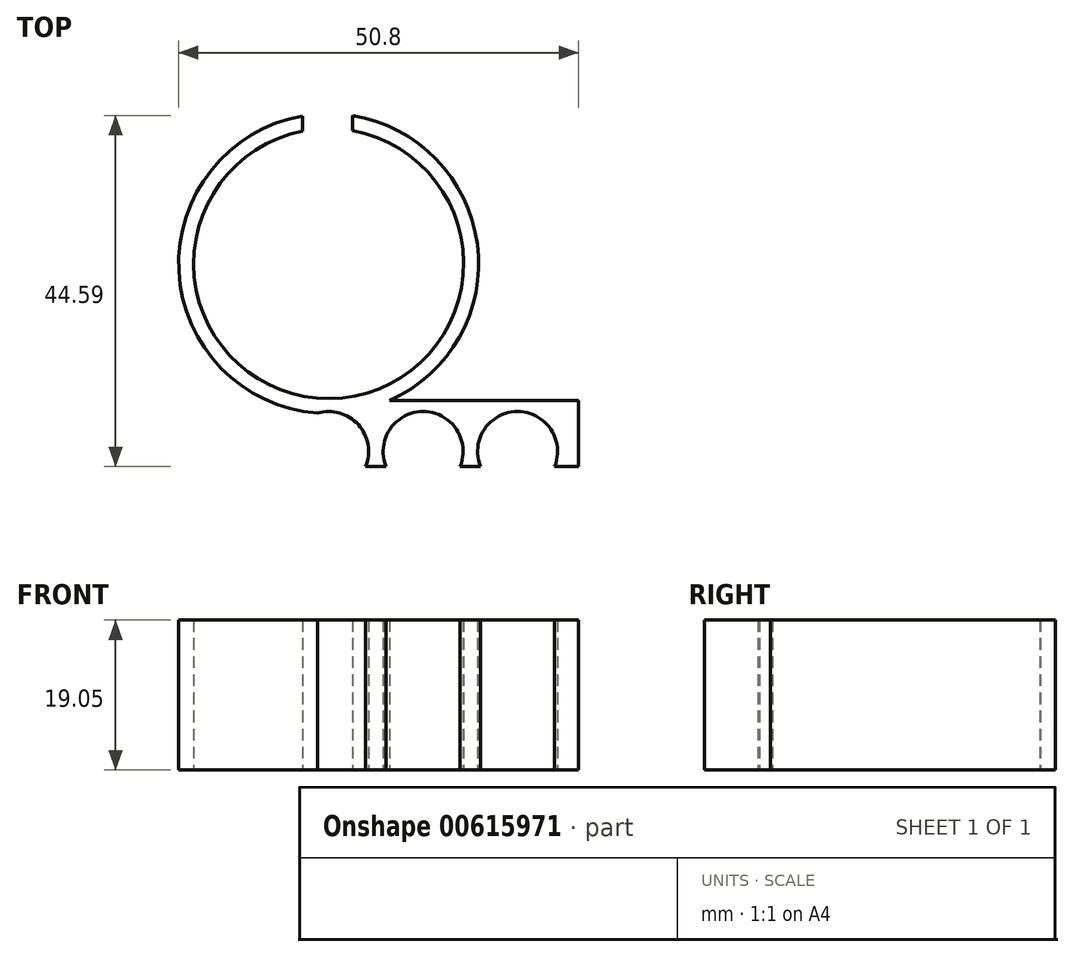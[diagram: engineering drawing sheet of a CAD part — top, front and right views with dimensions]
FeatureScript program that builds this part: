
annotation { "Feature Type Name" : "Feature", "Feature Type Description" : "" }
export const myFeature = defineFeature(function(context is Context, id is Id, definition is map)
    precondition{}
    {
        {
            var Q0;
            Q0=qCreatedBy(makeId("Top.planeOp"),FACE);
            var sketch = newSketch(context, id + "F0", { "sketchPlane" : qUnion([Q0])});
            skCircle(sketch, "E0", {"center": v(0, 0) * mm, "radius": 19.05 * mm});
            skCircle(sketch, "E1", {"center": v(0, 0) * mm, "radius": 17.15 * mm});
            skLineSegment(sketch, "E2.bottom", {"start": v(31.75, -17.4) * mm, "end": v(-31.75, -17.4) * mm});
            skLineSegment(sketch, "E2.top", {"start": v(31.75, -25.78) * mm, "end": v(-31.75, -25.78) * mm});
            skLineSegment(sketch, "E2.left", {"start": v(31.75, -17.4) * mm, "end": v(31.75, -25.78) * mm});
            skLineSegment(sketch, "E2.right", {"start": v(-31.75, -17.4) * mm, "end": v(-31.75, -25.78) * mm});
            skPoint(sketch, "E2.middle", {"position": v(0, -21.59) * mm});
            skCircle(sketch, "E3", {"center": v(0, -23.88) * mm, "radius": 5.08 * mm});
            skPoint(sketch, "E3.centerSnap0", {"position": v(0, -25.78) * mm});
            skCircle(sketch, "E4.1.0.0", {"center": v(12, -23.88) * mm, "radius": 5.08 * mm});
            skCircle(sketch, "E4.2.0.0", {"center": v(24, -23.88) * mm, "radius": 5.08 * mm});
            skLineSegment(sketch, "E4.direction1", {"start": v(0, -23.88) * mm, "end": v(12, -23.88) * mm, "construction": true});
            skCircle(sketch, "E5.1.0.0", {"center": v(-12, -23.88) * mm, "radius": 5.08 * mm});
            skCircle(sketch, "E5.2.0.0", {"center": v(-24, -23.88) * mm, "radius": 5.08 * mm});
            skLineSegment(sketch, "E5.direction1", {"start": v(0, -23.88) * mm, "end": v(-12, -23.88) * mm, "construction": true});
            skSolve(sketch);
        }
        {
            var Q0;
            Q0=makeQuery(id+"F0.imprint","IMPRINT",FACE,{"disambiguationData":[TD([[makeQuery(id+"F0.imprint","IMPRINT",EDGE,{"derivedFrom":sQuery(id+"F0.wireOp",EDGE,"E1")}),-1.0]])]});
            var Q1;
            {var subQ0=sQuery(id+"F0.wireOp",EDGE,"E2.bottom");var subQ1=sQuery(id+"F0.wireOp",EDGE,"E0");var subQ2=makeQuery(id+"F0.imprint","INTERSECT",VERTEX,{"disambiguationData":[OD(0.0)],"derivedFrom":[subQ1,subQ0]});Q1=makeQuery(id+"F0.imprint","IMPRINT",FACE,{"disambiguationData":[TD([[makeQuery(id+"F0.imprint","IMPRINT",EDGE,{"disambiguationData":[TD([[subQ2,-1.0]])],"derivedFrom":subQ1}),1.0]])]});}
            var Q2;
            {var subQ0=sQuery(id+"F0.wireOp",EDGE,"E2.left");Q2=makeQuery(id+"F0.imprint","IMPRINT",FACE,{"disambiguationData":[TD([[makeQuery(id+"F0.imprint","IMPRINT",EDGE,{"derivedFrom":subQ0}),-1.0]])]});}
            var Q3;
            {var subQ8=sQuery(id+"F0.wireOp",EDGE,"E2.right");Q3=makeQuery(id+"F0.imprint","IMPRINT",FACE,{"disambiguationData":[TD([[makeQuery(id+"F0.imprint","IMPRINT",EDGE,{"derivedFrom":subQ8}),1.0]])]});}
            extrude(context, id + "F1", {"entities" : qUnion([Q0, Q1, Q2, Q3]), "depth" : 19.05 * mm, "offsetDistance" : 25 * mm});
        }
        {
            var Q0;
            {var subQ0=sQuery(id+"F0.wireOp",EDGE,"E4.3.0.0");var subQ1=sQuery(id+"F0.wireOp",EDGE,"E2.top");var subQ2=makeQuery(id+"F0.imprint","INTERSECT",VERTEX,{"disambiguationData":[OD(0.0)],"derivedFrom":[subQ1,subQ0]});Q0=makeQuery(id+"F0.imprint","IMPRINT",FACE,{"disambiguationData":[TD([[makeQuery(id+"F0.imprint","IMPRINT",EDGE,{"disambiguationData":[TD([[subQ2,-1.0]])],"derivedFrom":subQ1}),-1.0]])]});}
            var Q1;
            {var subQ0=sQuery(id+"F0.wireOp",EDGE,"E4.2.0.0");var subQ1=sQuery(id+"F0.wireOp",EDGE,"E2.top");var subQ2=makeQuery(id+"F0.imprint","INTERSECT",VERTEX,{"disambiguationData":[OD(0.0)],"derivedFrom":[subQ1,subQ0]});Q1=makeQuery(id+"F0.imprint","IMPRINT",FACE,{"disambiguationData":[TD([[makeQuery(id+"F0.imprint","IMPRINT",EDGE,{"disambiguationData":[TD([[subQ2,-1.0]])],"derivedFrom":subQ1}),-1.0]])]});}
            var Q2;
            {var subQ0=sQuery(id+"F0.wireOp",EDGE,"E4.1.0.0");var subQ1=sQuery(id+"F0.wireOp",EDGE,"E2.top");var subQ2=makeQuery(id+"F0.imprint","INTERSECT",VERTEX,{"disambiguationData":[OD(0.0)],"derivedFrom":[subQ1,subQ0]});Q2=makeQuery(id+"F0.imprint","IMPRINT",FACE,{"disambiguationData":[TD([[makeQuery(id+"F0.imprint","IMPRINT",EDGE,{"disambiguationData":[TD([[subQ2,-1.0]])],"derivedFrom":subQ1}),-1.0]])]});}
            var Q3;
            {var subQ0=sQuery(id+"F0.wireOp",EDGE,"E3");var subQ1=sQuery(id+"F0.wireOp",EDGE,"E2.top");var subQ2=makeQuery(id+"F0.imprint","INTERSECT",VERTEX,{"disambiguationData":[OD(0.0)],"derivedFrom":[subQ1,subQ0]});Q3=makeQuery(id+"F0.imprint","IMPRINT",FACE,{"disambiguationData":[TD([[makeQuery(id+"F0.imprint","IMPRINT",EDGE,{"disambiguationData":[TD([[subQ2,-1.0]])],"derivedFrom":subQ1}),-1.0]])]});}
            var Q4;
            {var subQ0=sQuery(id+"F0.wireOp",EDGE,"E5.1.0.0");var subQ1=sQuery(id+"F0.wireOp",EDGE,"E2.top");var subQ2=makeQuery(id+"F0.imprint","INTERSECT",VERTEX,{"disambiguationData":[OD(0.0)],"derivedFrom":[subQ1,subQ0]});Q4=makeQuery(id+"F0.imprint","IMPRINT",FACE,{"disambiguationData":[TD([[makeQuery(id+"F0.imprint","IMPRINT",EDGE,{"disambiguationData":[TD([[subQ2,-1.0]])],"derivedFrom":subQ1}),-1.0]])]});}
            var Q5;
            {var subQ0=sQuery(id+"F0.wireOp",EDGE,"E5.2.0.0");var subQ1=sQuery(id+"F0.wireOp",EDGE,"E2.top");var subQ2=makeQuery(id+"F0.imprint","INTERSECT",VERTEX,{"disambiguationData":[OD(0.0)],"derivedFrom":[subQ1,subQ0]});Q5=makeQuery(id+"F0.imprint","IMPRINT",FACE,{"disambiguationData":[TD([[makeQuery(id+"F0.imprint","IMPRINT",EDGE,{"disambiguationData":[TD([[subQ2,-1.0]])],"derivedFrom":subQ1}),-1.0]])]});}
            var Q6;
            {var subQ0=sQuery(id+"F0.wireOp",EDGE,"E5.3.0.0");var subQ1=sQuery(id+"F0.wireOp",EDGE,"E2.top");var subQ2=makeQuery(id+"F0.imprint","INTERSECT",VERTEX,{"disambiguationData":[OD(0.0)],"derivedFrom":[subQ1,subQ0]});Q6=makeQuery(id+"F0.imprint","IMPRINT",FACE,{"disambiguationData":[TD([[makeQuery(id+"F0.imprint","IMPRINT",EDGE,{"disambiguationData":[TD([[subQ2,-1.0]])],"derivedFrom":subQ1}),-1.0]])]});}
            var Q7;
            Q7=sQuery(id+"F0.wireOp",EDGE,"E5.3.0.0");
            var Q8;
            Q8=sQuery(id+"F0.wireOp",EDGE,"E5.2.0.0");
            var Q9;
            Q9=sQuery(id+"F0.wireOp",EDGE,"E5.1.0.0");
            var Q10;
            Q10=sQuery(id+"F0.wireOp",EDGE,"E3");
            var Q11;
            Q11=sQuery(id+"F0.wireOp",EDGE,"E4.1.0.0");
            var Q12;
            Q12=sQuery(id+"F0.wireOp",EDGE,"E4.2.0.0");
            var Q13;
            Q13=sQuery(id+"F0.wireOp",EDGE,"E4.3.0.0");
            extrude(context, id + "F2", {"entities" : qUnion([Q0, Q1, Q2, Q3, Q4, Q5, Q6]), "operationType" : NewBodyOperationType.REMOVE, "surfaceEntities" : qUnion([Q7, Q8, Q9, Q10, Q11, Q12, Q13]), "depth" : 25.4 * mm});
        }
        {
            var Q0;
            Q0=qCreatedBy(makeId("Top.planeOp"),FACE);
            var sketch = newSketch(context, id + "F3", { "sketchPlane" : qUnion([Q0])});
            skLineSegment(sketch, "E6.bottom", {"start": v(-3.31, 0) * mm, "end": v(3.04, 0) * mm});
            skLineSegment(sketch, "E6.top", {"start": v(-3.31, 30.1) * mm, "end": v(3.04, 30.1) * mm});
            skLineSegment(sketch, "E6.left", {"start": v(-3.31, 0) * mm, "end": v(-3.31, 30.1) * mm});
            skLineSegment(sketch, "E6.right", {"start": v(3.04, 0) * mm, "end": v(3.04, 30.1) * mm});
            skSolve(sketch);
        }
        {
            var Q0;
            Q0=qSketchRegion(id+"F3",true);
            extrude(context, id + "F4", {"entities" : qUnion([Q0]), "operationType" : NewBodyOperationType.REMOVE, "depth" : 25.4 * mm});
        }
    });
